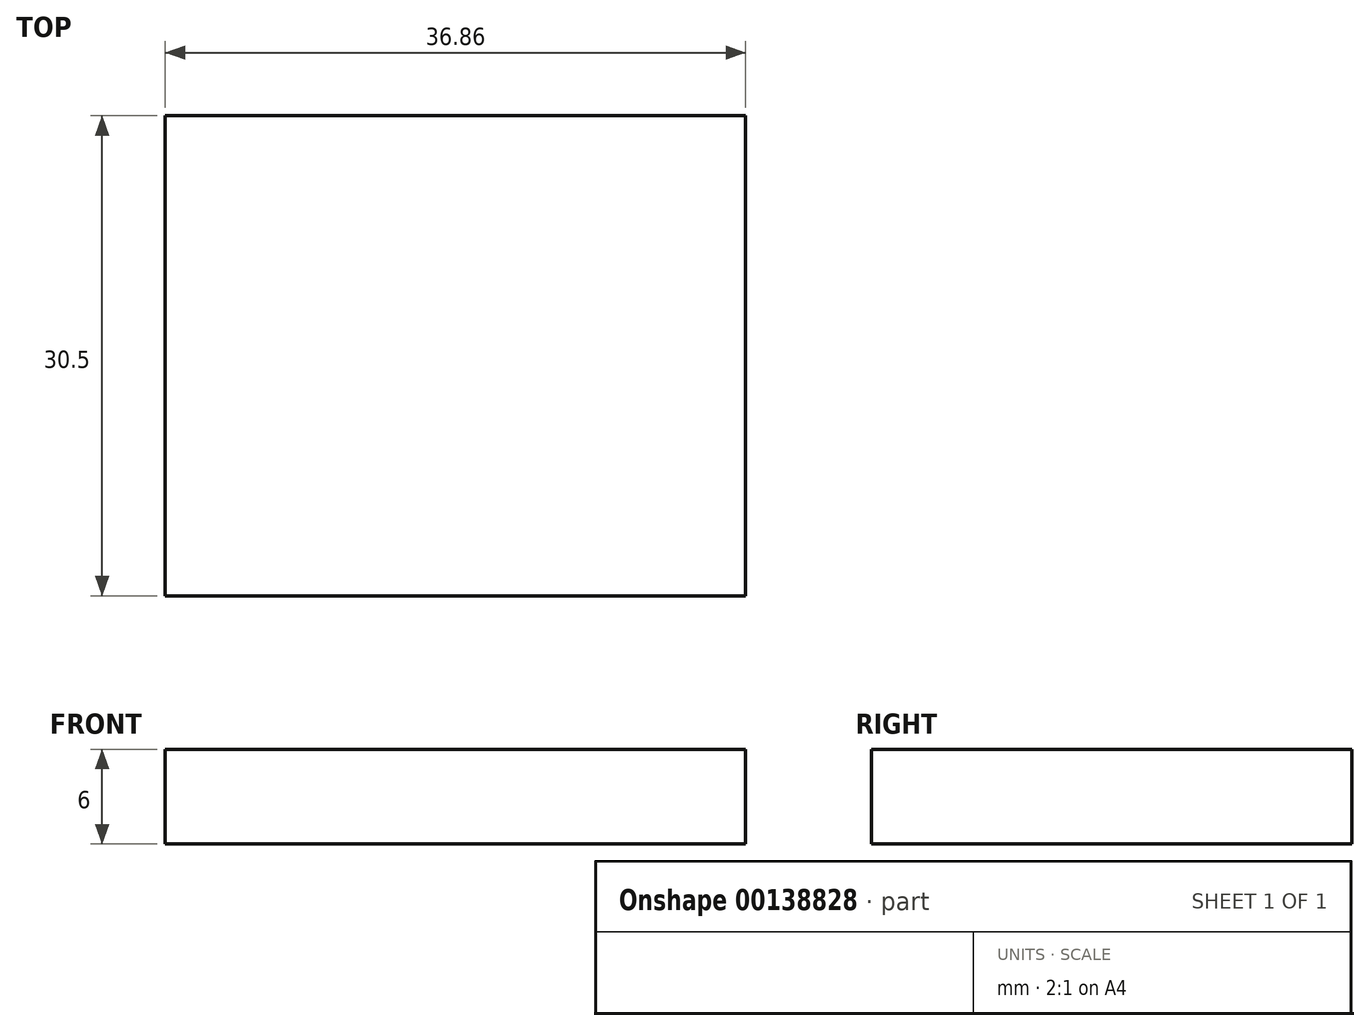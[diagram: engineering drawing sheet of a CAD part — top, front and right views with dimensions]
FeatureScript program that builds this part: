
annotation { "Feature Type Name" : "Feature", "Feature Type Description" : "" }
export const myFeature = defineFeature(function(context is Context, id is Id, definition is map)
    precondition{}
    {
        {
            var Q0;
            Q0=qCreatedBy(makeId("Top.planeOp"),FACE);
            var sketch = newSketch(context, id + "F0", { "sketchPlane" : qUnion([Q0])});
            skLineSegment(sketch, "E0.bottom", {"start": v(18.43, 15.25) * mm, "end": v(-18.43, 15.25) * mm});
            skLineSegment(sketch, "E0.top", {"start": v(18.43, -15.25) * mm, "end": v(-18.43, -15.25) * mm});
            skLineSegment(sketch, "E0.left", {"start": v(18.43, 15.25) * mm, "end": v(18.43, -15.25) * mm});
            skLineSegment(sketch, "E0.right", {"start": v(-18.43, 15.25) * mm, "end": v(-18.43, -15.25) * mm});
            skPoint(sketch, "E0.middle", {"position": v(0, 0) * mm});
            skSolve(sketch);
        }
        {
            var Q0;
            Q0 = qSketchRegion(id + "F0", true);
            extrude(context, id + "F1", {"entities" : qUnion([Q0]), "depth" : 6 * mm});
        }
    });
